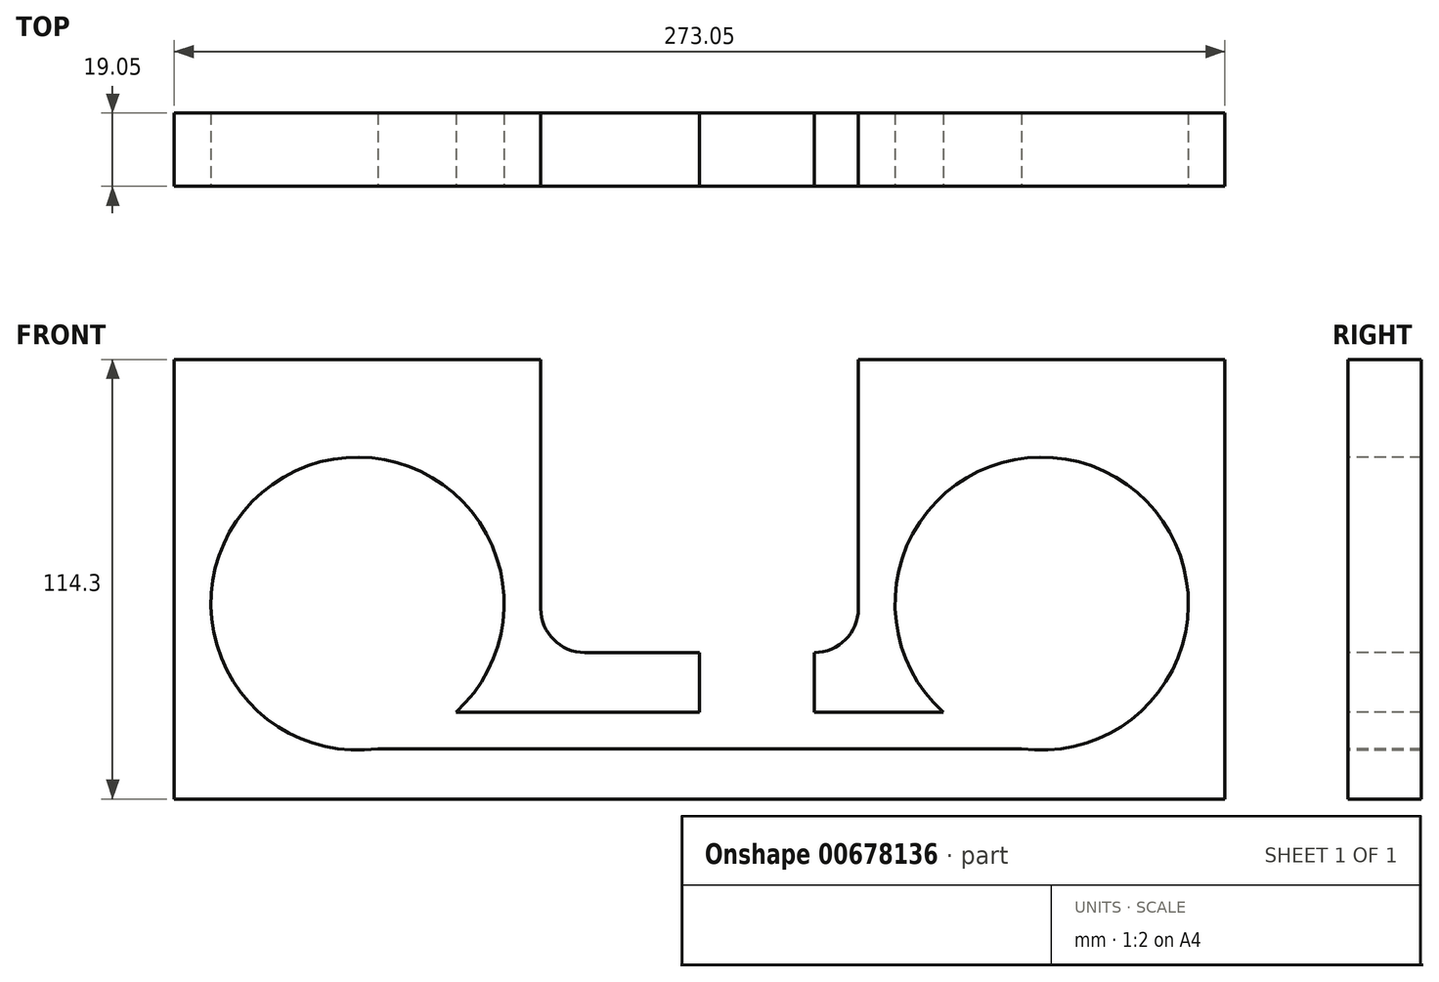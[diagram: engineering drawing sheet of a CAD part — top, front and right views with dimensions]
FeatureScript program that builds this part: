
annotation { "Feature Type Name" : "Feature", "Feature Type Description" : "" }
export const myFeature = defineFeature(function(context is Context, id is Id, definition is map)
    precondition{}
    {
        {
            var Q0;
            Q0=qCreatedBy(makeId("Front.planeOp"),FACE);
            var sketch = newSketch(context, id + "F0", { "sketchPlane" : qUnion([Q0])});
            skLineSegment(sketch, "E0.bottom", {"start": v(0, 0) * mm, "end": v(273.05, 0) * mm});
            skLineSegment(sketch, "E0.top", {"start": v(0, 114.3) * mm, "end": v(273.05, 114.3) * mm});
            skLineSegment(sketch, "E0.left", {"start": v(0, 0) * mm, "end": v(0, 114.3) * mm});
            skLineSegment(sketch, "E0.right", {"start": v(273.05, 0) * mm, "end": v(273.05, 114.3) * mm});
            skSolve(sketch);
        }
        {
            var Q0;
            Q0 = qSketchRegion(id + "F0", true);
            extrude(context, id + "F1", {"entities" : qUnion([Q0]), "depth" : 19.05 * mm, "offsetDistance" : 25.4 * mm});
        }
        {
            var Q0;
            Q0=makeQuery(id+"F1.opExtrude","CAP_FACE",FACE,{"disambiguationData":[OSD([sQuery(id+"F0.wireOp",EDGE,"E0.bottom"),sQuery(id+"F0.wireOp",EDGE,"E0.top"),sQuery(id+"F0.wireOp",EDGE,"E0.left"),sQuery(id+"F0.wireOp",EDGE,"E0.right")])],"isStart":false});
            var sketch = newSketch(context, id + "F2", { "sketchPlane" : qUnion([Q0])});
            skCircle(sketch, "E1", {"center": v(47.63, 50.8) * mm, "radius": 38.1 * mm});
            skCircle(sketch, "E2", {"center": v(225.43, 50.8) * mm, "radius": 38.1 * mm});
            skSolve(sketch);
        }
        {
            var Q0;
            Q0=makeQuery(id+"F2.imprint","IMPRINT",FACE,{"disambiguationData":[TD([[makeQuery(id+"F2.imprint","IMPRINT",EDGE,{"derivedFrom":sQuery(id+"F2.wireOp",EDGE,"E2")}),1.0]])]});
            var Q1;
            Q1=makeQuery(id+"F2.imprint","IMPRINT",FACE,{"disambiguationData":[TD([[makeQuery(id+"F2.imprint","IMPRINT",EDGE,{"derivedFrom":sQuery(id+"F2.wireOp",EDGE,"E1")}),1.0]])]});
            extrude(context, id + "F3", {"entities" : qUnion([Q0, Q1]), "operationType" : NewBodyOperationType.REMOVE, "oppositeDirection" : true, "depth" : 25.4 * mm, "offsetDistance" : 25.4 * mm});
        }
        {
            var Q0;
            Q0=makeQuery(id+"F1.opExtrude","CAP_FACE",FACE,{"disambiguationData":[OSD([sQuery(id+"F0.wireOp",EDGE,"E0.bottom"),sQuery(id+"F0.wireOp",EDGE,"E0.top"),sQuery(id+"F0.wireOp",EDGE,"E0.left"),sQuery(id+"F0.wireOp",EDGE,"E0.right")])],"isStart":false});
            var sketch = newSketch(context, id + "F4", { "sketchPlane" : qUnion([Q0])});
            skLineSegment(sketch, "E3", {"start": v(95.25, 114.3) * mm, "end": v(95.25, 49.53) * mm});
            skLineSegment(sketch, "E4", {"start": v(106.68, 38.1) * mm, "end": v(166.37, 38.1) * mm});
            skLineSegment(sketch, "E5", {"start": v(177.8, 49.53) * mm, "end": v(177.8, 114.3) * mm});
            skPoint(sketch, "E6.visualSharp", {"position": v(95.25, 38.1) * mm});
            skArc(sketch, "E6.filletArc", {"start": v(95.25, 49.53) * mm, "mid": v(98.6, 41.45) * mm, "end": v(106.68, 38.1) * mm});
            skPoint(sketch, "E7.visualSharp", {"position": v(177.8, 38.1) * mm});
            skArc(sketch, "E7.filletArc", {"start": v(166.37, 38.1) * mm, "mid": v(174.45, 41.45) * mm, "end": v(177.8, 49.53) * mm});
            skSolve(sketch);
        }
        {
            var Q0;
            {var subQ1=sQuery(id+"F4.wireOp",EDGE,"E3");Q0=makeQuery(id+"F4.imprint","IMPRINT",FACE,{"disambiguationData":[TD([[makeQuery(id+"F4.imprint","IMPRINT",EDGE,{"derivedFrom":subQ1}),1.0]])]});}
            extrude(context, id + "F5", {"entities" : qUnion([Q0]), "operationType" : NewBodyOperationType.REMOVE, "oppositeDirection" : true, "depth" : 25.4 * mm, "offsetDistance" : 25.4 * mm});
        }
        {
            var Q0;
            Q0=makeQuery(id+"F1.opExtrude","CAP_FACE",FACE,{"disambiguationData":[OSD([sQuery(id+"F0.wireOp",EDGE,"E0.bottom"),sQuery(id+"F0.wireOp",EDGE,"E0.top"),sQuery(id+"F0.wireOp",EDGE,"E0.left"),sQuery(id+"F0.wireOp",EDGE,"E0.right")])],"isStart":false});
            var sketch = newSketch(context, id + "F6", { "sketchPlane" : qUnion([Q0])});
            skLineSegment(sketch, "E8", {"start": v(166.37, 38.1) * mm, "end": v(136.53, 38.1) * mm});
            skLineSegment(sketch, "E9", {"start": v(136.53, 38.1) * mm, "end": v(136.53, 22.6) * mm});
            skLineSegment(sketch, "E10", {"start": v(136.53, 22.6) * mm, "end": v(54.54, 22.6) * mm});
            skLineSegment(sketch, "E11", {"start": v(166.37, 38.1) * mm, "end": v(166.37, 22.6) * mm});
            skLineSegment(sketch, "E12", {"start": v(166.37, 22.6) * mm, "end": v(218.82, 22.6) * mm});
            skLineSegment(sketch, "E13", {"start": v(218.82, 22.6) * mm, "end": v(230.69, 13.07) * mm});
            skLineSegment(sketch, "E14", {"start": v(230.69, 13.07) * mm, "end": v(42.36, 13.07) * mm});
            skLineSegment(sketch, "E15", {"start": v(42.36, 13.07) * mm, "end": v(54.54, 22.6) * mm});
            skSolve(sketch);
        }
        {
            var Q0;
            Q0=makeQuery(id+"F6.imprint","IMPRINT",FACE,{"disambiguationData":[TD([[makeQuery(id+"F6.imprint","IMPRINT",EDGE,{"derivedFrom":sQuery(id+"F6.wireOp",EDGE,"E8")}),-1.0]])]});
            extrude(context, id + "F7", {"entities" : qUnion([Q0]), "operationType" : NewBodyOperationType.REMOVE, "oppositeDirection" : true, "depth" : 25.4 * mm, "offsetDistance" : 25.4 * mm});
        }
    });
